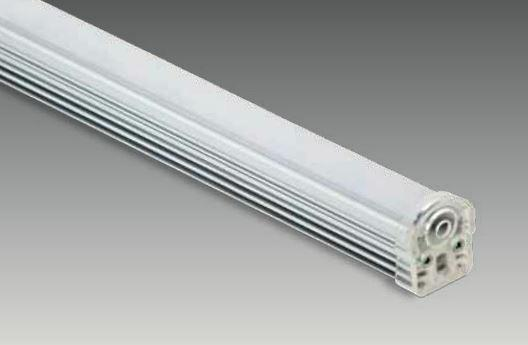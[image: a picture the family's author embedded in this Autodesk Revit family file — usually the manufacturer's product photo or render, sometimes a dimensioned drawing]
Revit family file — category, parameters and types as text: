
# Revit family: SD 1000 CVK
name_source: partatom
category: Lighting Fixtures
revit_build: Autodesk Revit 2017 (Build: 20160225_1515(x64)
units: mm (PartAtom-declared; Revit-internal decimal feet)

## family parameters
Cut with Voids When Loaded = No
Host = Face
Light Source = Yes
Part Type = Normal
Room Calculation Point = No
Round Connector Dimension = Use Diameter
Shared = No

## types (2) — shared parameters
Apparent Load = 24 VA
Color Filter = 16777215
Default Elevation = 1219 mm
Dimming Lamp Color Temperature Shift = <None>
Emit Shape Visible in Rendering = Yes
Emit from Rectangle Length = 15 mm  [stored 0.0492126 ft]
Emit from Rectangle Width = 1000 mm  [stored 3.28084 ft]
Light Source Symbol Size = 610 mm
Manufacturer = ARLIGHT
Type Image = SD 1000 CVK.JPG
Wattage Comments = 24

## type names (no varying parameters)
- SDCVK.1000.24.30
- SDCVK.1000.24.40

note: [stored X ft] marks values corroborated as IEEE doubles in the binary element streams (Revit-internal decimal feet)

## geometry (parser evidence)
native form markers: Sweep x3
no freeform markers — native parametric forms only
